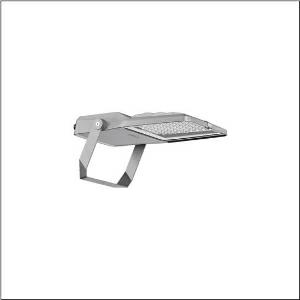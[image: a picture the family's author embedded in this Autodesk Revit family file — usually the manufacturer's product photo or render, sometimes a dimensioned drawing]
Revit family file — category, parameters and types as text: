
# Revit family: floodlight_fl_21_iq_mini___pl61_5xa7772b4c1a_1528
name_source: partatom
category: Lighting Fixtures
units: mm (PartAtom-declared; Revit-internal decimal feet)

## family parameters
Cut with Voids When Loaded = No
Host = Face
Light Source = No
Part Type = Normal
Room Calculation Point = No
Round Connector Dimension = Use Diameter
Shared = No

## types (1)
- --- (1 x LED, 6370 lm, 45.5 W, 4000K)
    Apparent Load = 46 VA
    CIE Flux Codes = 33 65 98 100 100
    Color Rendering = 70
    Color Temperature = 4000K
    Default Elevation = 1800 mm
    Description = Floodlight FL 21 iQ mini, floodlight, primary light control with lens, of PMMA, primary optical cover: protective disc, of toughened safety glass, transparent, light distribution: PL61, light emission: direct distribution, installation type: surface-mounted, LED, High Power LED, rated luminous flux: 6.370lm, luminous efficacy: 140lm/W, light colour: 740, colour temperature: 4000K, control gear: iQ Street-Remote/DALI, control: Street-Remote, Auto-Match, Temp-Guard, Night-Set, Smart-Wire, Desk-Remote (wireless, voltage-free reading and setting of iQ features in the workshop via application-optimized NFC function/RFID function), optimised constant luminous flux control (CLO 2.0), with terminal, 6-pole, mains connection: 220..240V, AC, 50/60Hz, start of lifetime: 46W, end of service life: 48W, reduction: 22W, luminaire housing, of diecast aluminium, powder-coated, Siteco® metallic grey (DB 702S), corrosivity category C5 mid according to DIN EN ISO 12944, suitable for swimming pools, chlorine-resistant, sealing non-destructively replaceable, mounting bracket, of steel, galvanised, powder-coated, Siteco® metallic grey (DB 702S), protection rating (complete): IP66, insulation class (complete): insulation class II (safety insulation), certification: CE, ENEC, VDE, protection symbol: D, impact resistance: IK08, permissible operating ambient temperature: -40..+40°C, permissible operating ambient temperature for outdoor applications: -40..+50°C, standard: DIN EN 12944, LABS conformity tested according to VDMA 24364:2018-05, packaging unit: 1 piece

Light Distribution: PL61
    Height = 70 mm
    Lamp = 1 x LED
    Lamp Light Flux = 6370 lm
    Lamp Power = 45.5 W
    Lamp count = 1
    Length = 485 mm
    Luminous efficacy = 140 lm/W
    Manufacturer = Siteco
    ModVariant = No
    Model = 5XA7772B4C1A
    Number of Poles = 1
    OnlyDefault = Yes
    Power Factor = 1
    Product Name = Floodlight FL 21 iQ mini | PL61
    Product group = floodlight | pylon annexe
    ProductGroupID = 6200
    Protection Class = Protection class II
    Protection Degree = IP 66
    RLX_Detail_Level = 1
    RLX_Emergency_Light_Flux = 0 lm
    RLX_Emergency_Type = 0
    RLX_Emergency_Type_DB = No
    RlxData = <blob elided: 96285 chars, md5=3cd35548>
    Socket = socket
    Standby Power = 0 W
    System Light Flux = 6370 lm
    System Power = 46 W
    Type Comments = factory setting: luminous flux: 100 % | dim-lin: 254 | 463 mA
    Type Image = l_1006845.jpg
    URL = http://relux.com
    VarID = @adj_173512
    Voltage = 0 V
    Weight = 0.00 kg
    Width = 337 mm

## geometry (parser evidence)
native form markers: Blend x4, Sweep x12
no freeform markers — native parametric forms only
